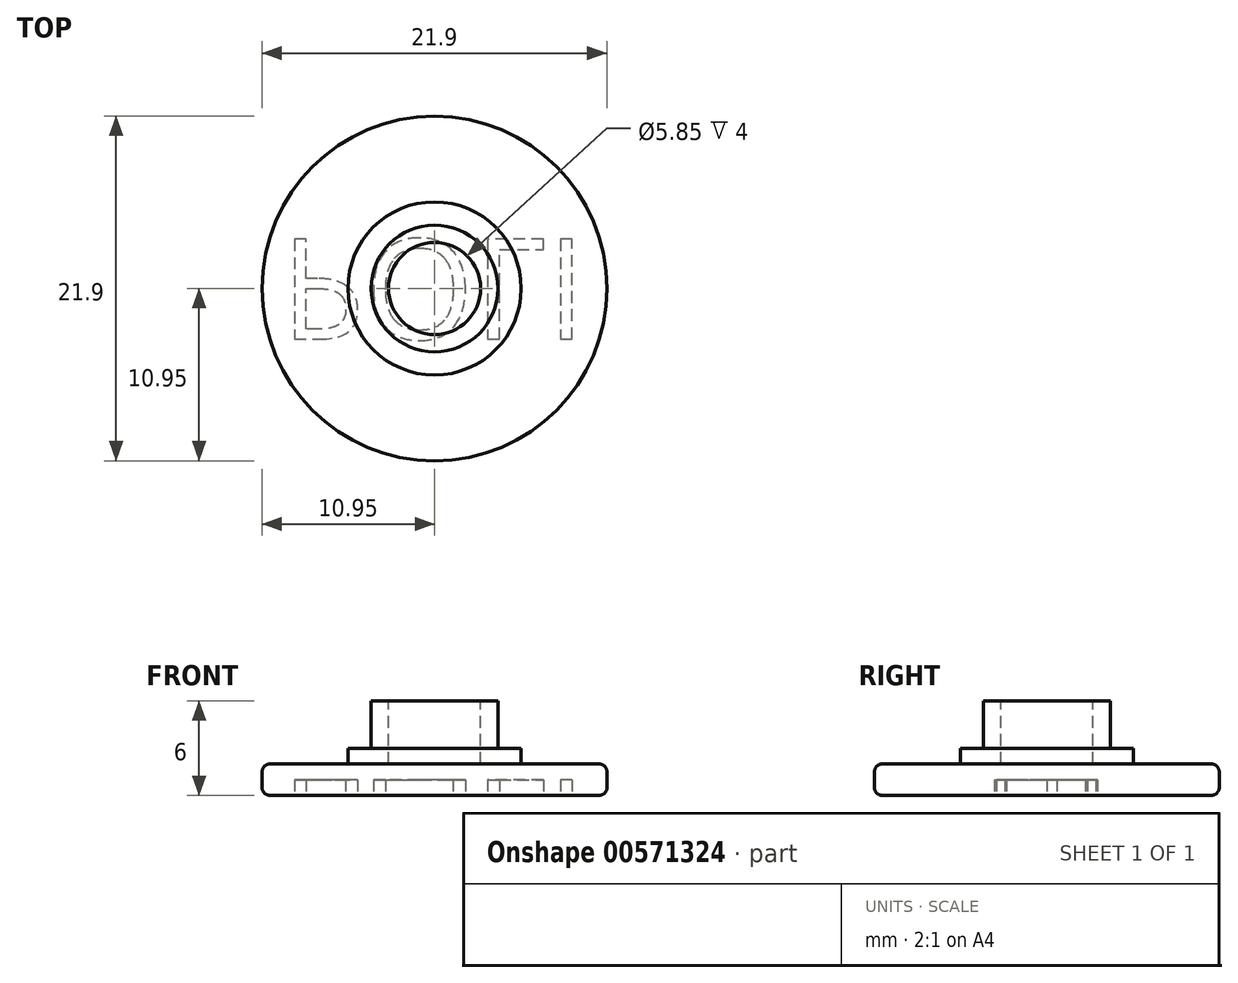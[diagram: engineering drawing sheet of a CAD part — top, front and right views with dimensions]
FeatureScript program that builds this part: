
annotation { "Feature Type Name" : "Feature", "Feature Type Description" : "" }
export const myFeature = defineFeature(function(context is Context, id is Id, definition is map)
    precondition{}
    {
        {
            var Q0;
            Q0=qCreatedBy(makeId("Top.planeOp"),FACE);
            var sketch = newSketch(context, id + "F0", { "sketchPlane" : qUnion([Q0])});
            skCircle(sketch, "E0", {"center": v(0, 0) * mm, "radius": 0.07 * mm});
            skCircle(sketch, "E1", {"center": v(0, 0) * mm, "radius": 10.95 * mm});
            skSolve(sketch);
        }
        {
            var Q0;
            Q0=qCreatedBy(makeId("Top.planeOp"),FACE);
            var sketch = newSketch(context, id + "F1", { "sketchPlane" : qUnion([Q0])});
            skCircle(sketch, "E2", {"center": v(0, 0) * mm, "radius": 5.5 * mm});
            skSolve(sketch);
        }
        {
            var Q0;
            Q0=qCreatedBy(makeId("Top.planeOp"),FACE);
            var sketch = newSketch(context, id + "F2", { "sketchPlane" : qUnion([Q0])});
            skCircle(sketch, "E3", {"center": v(0, 0) * mm, "radius": 4.03 * mm});
            skSolve(sketch);
        }
        {
            var Q0;
            Q0=qSketchRegion(id+"F0",true);
            extrude(context, id + "F3", {"entities" : qUnion([Q0]), "depth" : 2 * mm});
        }
        {
            var Q0;
            Q0=qSketchRegion(id+"F1",true);
            extrude(context, id + "F4", {"entities" : qUnion([Q0]), "operationType" : NewBodyOperationType.ADD, "depth" : 3 * mm, "offsetDistance" : 25 * mm});
        }
        {
            var Q0;
            Q0=qSketchRegion(id+"F2",true);
            extrude(context, id + "F5", {"entities" : qUnion([Q0]), "operationType" : NewBodyOperationType.ADD, "depth" : 6 * mm});
        }
        {
            var Q0;
            Q0=makeQuery(id+"F3.opExtrude","SWEPT_FACE",FACE,{"disambiguationData":[OSD([sQuery(id+"F0.wireOp",EDGE,"E1")])]});
            fillet(context, id + "F6", {"entities" : qUnion([Q0]), "radius" : .5 * mm, "tangentPropagation" : true, "allowEdgeOverflow" : false});
        }
        {
            var Q0;
            Q0=makeQuery(id+"F5.opExtrude","CAP_FACE",FACE,{"disambiguationData":[OSD([sQuery(id+"F2.wireOp",EDGE,"E3")])],"isStart":false});
            var sketch = newSketch(context, id + "F7", { "sketchPlane" : qUnion([Q0])});
            skCircle(sketch, "E4.0", {"center": v(0, 0) * mm, "radius": 2.92 * mm});
            skSolve(sketch);
        }
        {
            var Q0;
            Q0=qSketchRegion(id+"F7",true);
            extrude(context, id + "F8", {"entities" : qUnion([Q0]), "operationType" : NewBodyOperationType.REMOVE, "oppositeDirection" : true, "depth" : 4 * mm});
        }
        {
            var Q0;
            Q0=makeQuery(id+"F4.boolean.opBoolean","MERGE",FACE,{"derivedFrom":[makeQuery(id+"F3.opExtrude","CAP_FACE",FACE,{"disambiguationData":[OSD([sQuery(id+"F0.wireOp",EDGE,"E0"),sQuery(id+"F0.wireOp",EDGE,"E1")])],"isStart":true}),makeQuery(id+"F4.opExtrude","CAP_FACE",FACE,{"disambiguationData":[OSD([sQuery(id+"F1.wireOp",EDGE,"E2")])],"isStart":true})]});
            var sketch = newSketch(context, id + "F9", { "sketchPlane" : qUnion([Q0])});
            skText(sketch, "E5", { "text": "POLI\n", "fontName": "OpenSans-Regular.ttf"});
            const initialGuessF9  = {"E5": [-0.00977, -0.00313, 1, 0, 0.0064]};
            skSetInitialGuess(sketch, initialGuessF9);
            skSolve(sketch);
        }
        {
            var Q0;
            Q0 = qSketchRegion(id + "F9", true);
            extrude(context, id + "F10", {"entities" : qUnion([Q0]), "operationType" : NewBodyOperationType.REMOVE, "oppositeDirection" : true, "depth" : 1 * mm, "offsetDistance" : 25 * mm});
        }
    });
